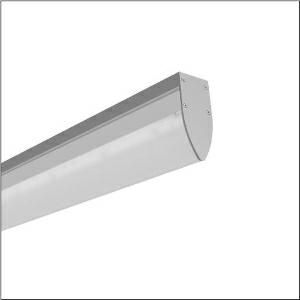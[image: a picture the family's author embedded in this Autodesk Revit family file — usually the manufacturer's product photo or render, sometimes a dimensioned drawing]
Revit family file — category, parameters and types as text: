
# Revit family: mira_r__21_td_51fr527k444a_1922
name_source: partatom
category: Lighting Fixtures
units: mm (PartAtom-declared; Revit-internal decimal feet)

## family parameters
Cut with Voids When Loaded = No
Host = Face
Light Source = No
Part Type = Normal
Room Calculation Point = No
Round Connector Dimension = Use Diameter
Shared = No

## types (1)
- Mira® 21 TD (1 x LED, 4030 lm, 27 W, 4000K)
    Apparent Load = 27 VA
    CIE Flux Codes = 40 68 87 81 100
    Color Rendering = 80
    Color Temperature = 4000K
    Default Elevation = 1800 mm
    Description = Mira® 21 TD, clean room luminaire, primary light control with reflector, primary optical cover: cover, of PMMA, frosted, light emission: direct distribution, primary light characteristic: symmetric, installation type: surface-mounted, LED, rated luminous flux: 4.030lm, luminous efficacy: 149lm/W, light colour: 840, colour temperature: 4000K, control gear: ON/OFF, with terminal, 3-pole, max. 2.5mm², mains connection: 230V, AC, 50/60Hz, rated input power: 27W, luminaire housing, of sheet steel, coated, pure white (RAL 9010), length: 1.200mm, width: 55mm, height: 120mm, protection rating (complete): IP43, insulation class (complete): insulation class I (protective earthing), certification: CE, UKCA, permissible operating ambient temperature: -5..+40°C, standard: EN 50419, packaging unit: 1 piece
    Height = 120 mm
    Lamp = 1 x LED
    Lamp Light Flux = 4030 lm
    Lamp Power = 27 W
    Lamp count = 1
    Length = 1200 mm
    Luminous efficacy = 149 lm/W
    Manufacturer = Siteco
    ModVariant = No
    Model = 51FR527K444A
    Mounting Place = Ceiling
    Mounting Type = Surface mounted
    Number of Poles = 1
    OnlyDefault = Yes
    Power Factor = 1
    Product Name = Mira® 21 TD
    Product group = clean room luminaire | ceiling mounted
    ProductGroupID = 305
    Protection Class = Protection class I
    Protection Degree = IP 43
    RLX_Detail_Level = 1
    RLX_Emergency_Light_Flux = 0 lm
    RLX_Emergency_Type = 0
    RLX_Emergency_Type_DB = No
    RlxData = <blob elided: 25193 chars, md5=b1a6f1c0>
    Socket = socket
    Standby Power = 0 W
    System Light Flux = 4030 lm
    System Power = 27 W
    Type Comments = Product without accessories
    Type Image = l_1007115.jpg
    URL = http://relux.com
    VarID = ---
    Voltage = 0 V
    Weight = 0.00 kg
    Width = 55 mm

## geometry (parser evidence)
native form markers: Blend x4, Sweep x13
no freeform markers — native parametric forms only
